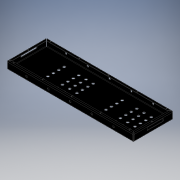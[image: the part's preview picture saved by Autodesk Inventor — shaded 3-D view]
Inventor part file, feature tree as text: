
AUTODESK INVENTOR PART (.ipt)
format: ipt  version: 2018 (Build 220112000, 112)  size: 601,600 bytes
history: native  units: in
note: dims shown in document units (in); Inventor stores cm internally (conversion verified against a paired STEP export)
features: thread x12, sketch x7, sheet_metal_op x7, extrude x4, other x4, projected_geometry x4, fillet x1
ambient origin geometry x8: Origin, YZ Plane, XZ Plane, XY Plane, X Axis, Y Axis, Z Axis, Center Point
bodies: Solid1 (feature_tree)
feature tree (39):
  sketch  "Sketch1"  dims[d0=0.75in d1=0.75in]
  sheet_metal_op  "Face1"
  extrude  "Extrusion1"  Depth=0.75in
  sheet_metal_op  "Flange3"
  sheet_metal_op  "Flange2"
  extrude  "Extrusion4"  Depth=0.062in
  thread  "Thread1"  [1 undecoded]
  thread  "Thread2"  [1 undecoded]
  thread  "Thread3"  [1 undecoded]
  thread  "Thread4"  [1 undecoded]
  thread  "Thread5"  [1 undecoded]
  thread  "Thread6"  [1 undecoded]
  thread  "Thread7"  [1 undecoded]
  thread  "Thread8"  [1 undecoded]
  thread  "Thread9"  [1 undecoded]
  thread  "Thread10"  [1 undecoded]
  thread  "Thread11"  [1 undecoded]
  thread  "Thread12"  [1 undecoded]
  extrude  "Extrusion3"  Depth=0.062in
  fillet  "Fillet1"  Radius=0.062in
  extrude  "Extrusion5"  Depth=0.124in
  sketch  "Sketch2"  dims[d2=0.062in d5=0.35in d7=1.9685in d9=0.75in d10=0.7874in d12=8.0in d15=1.0in d16=0.0in d27=0.062in d28=0.031in d29=0.124in d30=0.062in d31=0.35in d32=90.0deg d33=0.062in d34=0.248in d35=0.062in d36=0.062in d50=2.25in d51=0.375in]
  other  "Plate1"
  sketch  "Sketch3"  dims[d53=0.25in d54=0.0in d55=0.0625in d56=0.062in]
  sketch  "Sketch5"  dims[d57=0.031in d58=0.124in]
  other  "Plate3"
  sheet_metal_op  "Bend2"
  sheet_metal_op  "Corner2"
  sketch  "Sketch8"  dims[d59=0.062in]
  other  "Plate4"
  sheet_metal_op  "Bend3"
  sheet_metal_op  "Corner3"
  sketch  "Sketch9"  dims[d60=1.025in d61=90.0deg d62=0.062in]
  projected_geometry  "Projected Loop6"
  projected_geometry  "Projected Loop7"
  projected_geometry  "Projected Loop8"
  projected_geometry  "Projected Loop9"
  sketch  "Sketch10"  dims[d63=0.248in d64=0.062in d65=0.062in d68=0.13in d69=1.9685in d71=4.0in d72=0.7874in d74=5.075in d77=17.075in d79=0.25in d80=0.0in d81=0.375in d82=2.5in d83=0.275in d84=1.9685in d86=3.0in d87=0.3937in d89=1.0in d91=0.25in d92=0.0in d93=1.0in d94=0.0in d95=1.0in d96=0.0in d97=1.0in d98=0.0in d99=1.0in d100=0.0in d101=1.0in d102=0.0in d103=1.0in d104=0.0in d105=1.0in d106=0.0in d107=1.0in d108=0.0in d109=1.0in d110=0.0in d111=1.0in d112=0.0in d113=1.0in d114=0.0in d115=1.0in d116=0.0in]
  other  "Definition1"
note: 12 required parameter values undecoded (feature->parameter linkage not recoverable at this tier; creation-order binding heuristic only, values carry confidence <= 0.55)
